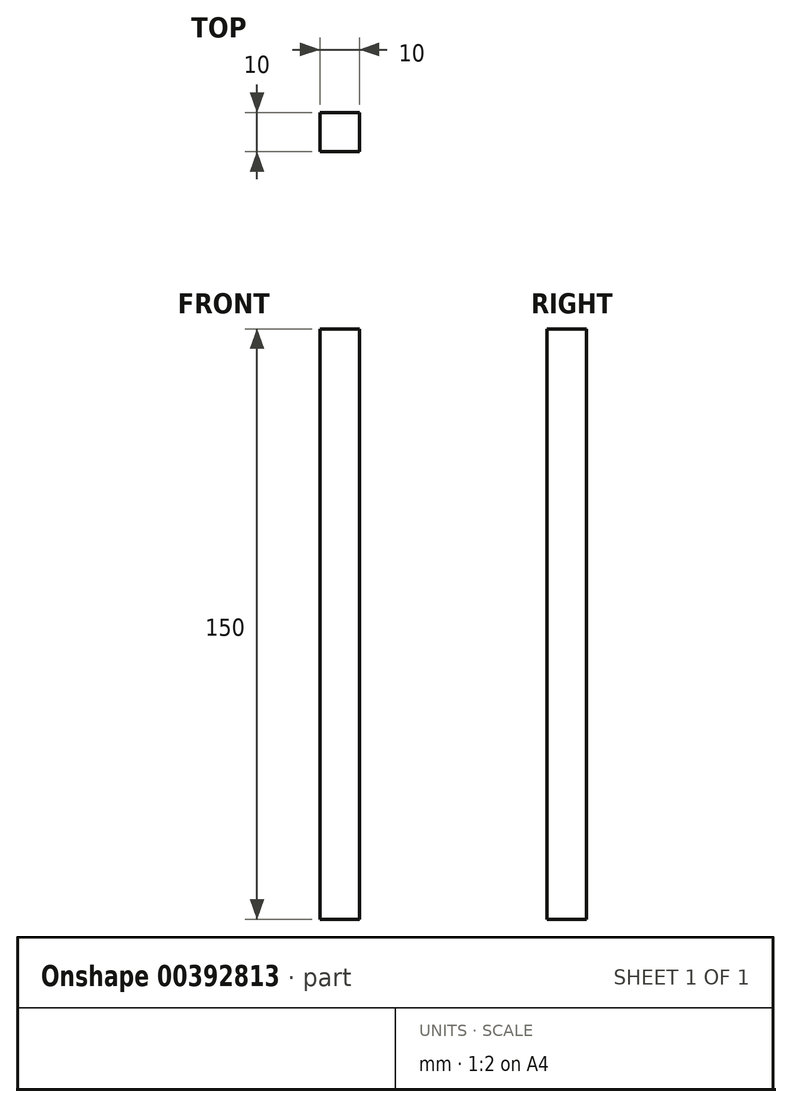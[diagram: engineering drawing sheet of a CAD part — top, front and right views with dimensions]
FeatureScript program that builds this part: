
annotation { "Feature Type Name" : "Feature", "Feature Type Description" : "" }
export const myFeature = defineFeature(function(context is Context, id is Id, definition is map)
    precondition{}
    {
        {
            var Q0;
            Q0=qCreatedBy(makeId("Top.planeOp"),FACE);
            var sketch = newSketch(context, id + "F0", { "sketchPlane" : qUnion([Q0])});
            skLineSegment(sketch, "E0.bottom", {"start": v(0, 0) * mm, "end": v(10, 0) * mm});
            skLineSegment(sketch, "E0.top", {"start": v(0, -10) * mm, "end": v(10, -10) * mm});
            skLineSegment(sketch, "E0.left", {"start": v(0, 0) * mm, "end": v(0, -10) * mm});
            skLineSegment(sketch, "E0.right", {"start": v(10, 0) * mm, "end": v(10, -10) * mm});
            skSolve(sketch);
        }
        {
            var Q0;
            Q0=qSketchRegion(id+"F0",true);
            extrude(context, id + "F1", {"entities" : qUnion([Q0]), "depth" : 150 * mm});
        }
    });
